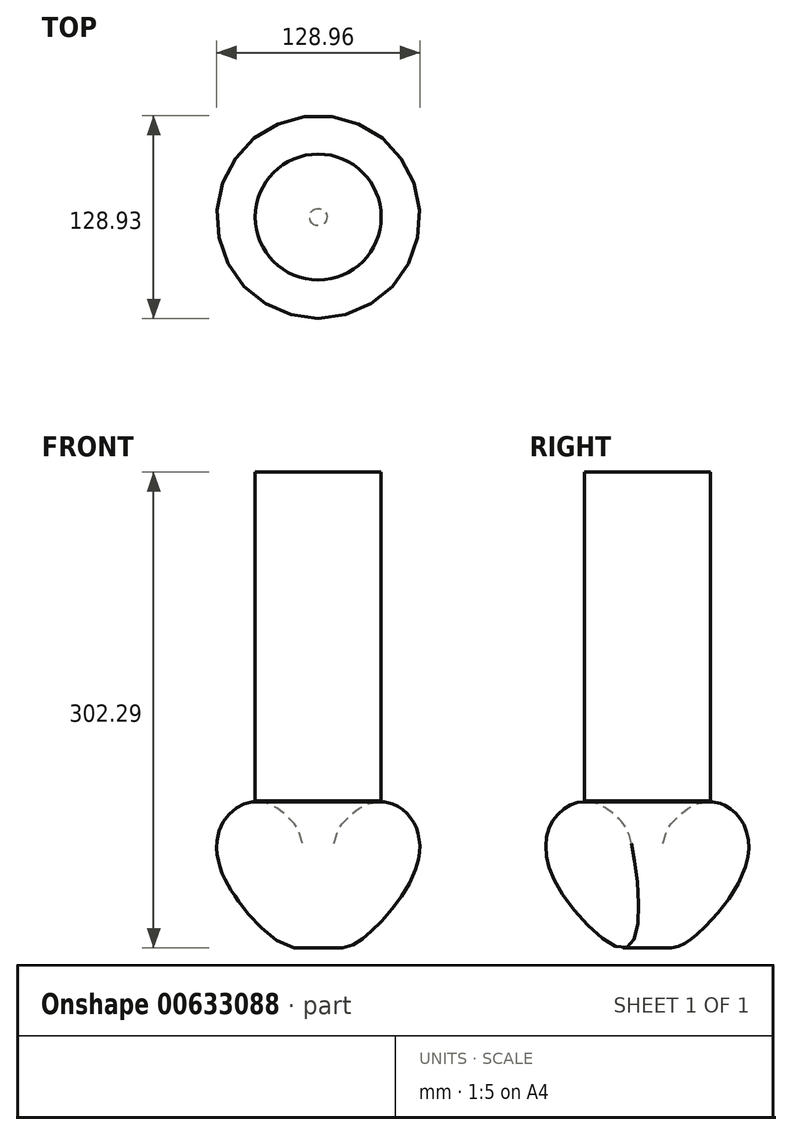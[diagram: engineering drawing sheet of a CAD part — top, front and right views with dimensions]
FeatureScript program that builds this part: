
annotation { "Feature Type Name" : "Feature", "Feature Type Description" : "" }
export const myFeature = defineFeature(function(context is Context, id is Id, definition is map)
    precondition{}
    {
        {
            var Q0;
            Q0=qCreatedBy(makeId("Top.planeOp"),FACE);
            var sketch = newSketch(context, id + "F0", { "sketchPlane" : qUnion([Q0])});
            skCircle(sketch, "E0", {"center": v(0, 0) * mm, "radius": 30 * mm});
            skSolve(sketch);
        }
        {
            var Q0;
            Q0=qCreatedBy(makeId("Right.planeOp"),FACE);
            var sketch = newSketch(context, id + "F1", { "sketchPlane" : qUnion([Q0])});
            skFitSpline(sketch, "E1", {"points": [v(-10.06, 14.97) * mm, v(-16.7, 29.25) * mm, v(-28.28, 38.64) * mm, v(-40.15, 41.46) * mm, v(-50.9, 38.44) * mm, v(-60.45, 28.7) * mm, v(-64.46, 13.79) * mm, v(-53.26, -17.92) * mm, v(-11.63, -50.24) * mm, v(-10.06, 14.97) * mm]});
            skSolve(sketch);
        }
        {
            var Q0;
            Q0=makeQuery(id+"F1.imprint","IMPRINT",FACE,{"disambiguationData":[TD([[makeQuery(id+"F1.imprint","IMPRINT",EDGE,{"derivedFrom":sQuery(id+"F1.wireOp",EDGE,"E1")}),1.0]])]});
            var Q1;
            Q1=sQuery(id+"F0.wireOp",EDGE,"E0");
            revolve(context, id + "F2", {"entities" : qUnion([Q0]), "axis" : qUnion([Q1]), "revolveType" : RevolveType.FULL});
        }
        {
            var Q0;
            Q0=qCreatedBy(makeId("Top.planeOp"),FACE);
            cPlane(context, id + "F3", {"entities" : qUnion([Q0]), "cplaneType" : CPlaneType.OFFSET, "offset" : 42 * mm, "width" : 150 * mm, "height" : 150 * mm});
        }
        {
            var Q0;
            Q0=qCreatedBy(id+"F3.planeOp",FACE);
            var sketch = newSketch(context, id + "F4", { "sketchPlane" : qUnion([Q0])});
            skCircle(sketch, "E2", {"center": v(0, 0) * mm, "radius": 40 * mm});
            skSolve(sketch);
        }
        {
            var Q0;
            Q0 = qSketchRegion(id + "F4", true);
            extrude(context, id + "F5", {"entities" : qUnion([Q0]), "operationType" : NewBodyOperationType.ADD, "depth" : 209 * mm, "offsetDistance" : 25 * mm});
        }
    });
